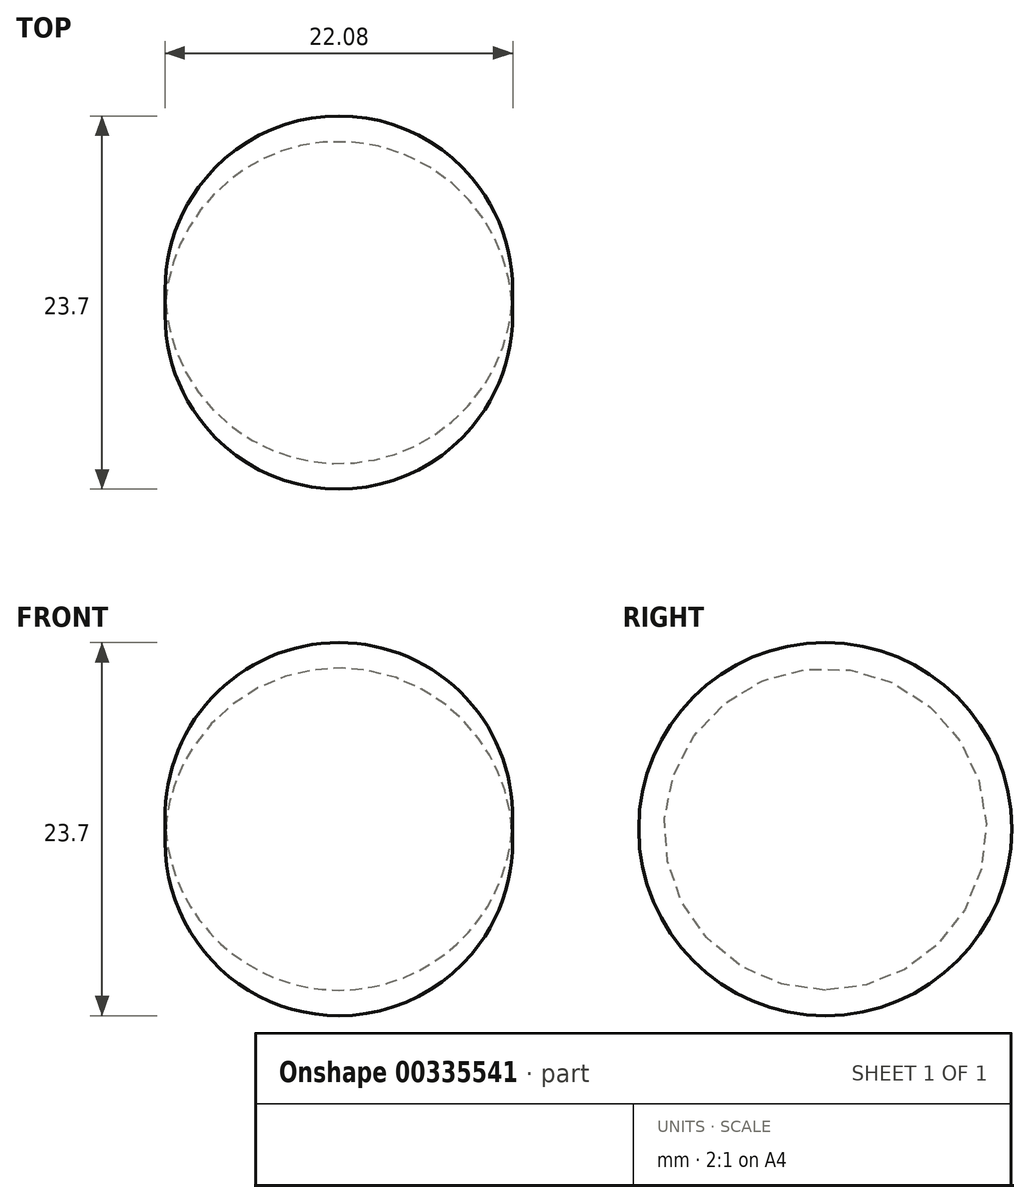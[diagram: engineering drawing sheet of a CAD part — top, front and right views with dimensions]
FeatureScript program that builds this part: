
annotation { "Feature Type Name" : "Feature", "Feature Type Description" : "" }
export const myFeature = defineFeature(function(context is Context, id is Id, definition is map)
    precondition{}
    {
        {
            var Q0;
            Q0=qCreatedBy(makeId("Front.planeOp"),FACE);
            var sketch = newSketch(context, id + "F0", { "sketchPlane" : qUnion([Q0])});
            skLineSegment(sketch, "E0", {"start": v(-11.26, 0) * mm, "end": v(10.77, 0) * mm});
            skLineSegment(sketch, "E1", {"start": v(10.77, 0) * mm, "end": v(-11.26, 0) * mm});
            skPoint(sketch, "E2.orphan", {"position": v(-18.6, 0) * mm});
            skArc(sketch, "E3", {"start": v(10.77, 0) * mm, "mid": v(-0.24, 11.85) * mm, "end": v(-11.26, 0) * mm});
            skSolve(sketch);
        }
        {
            var Q0;
            Q0=makeQuery(id+"F0.imprint","IMPRINT",FACE,{"disambiguationData":[TD([[makeQuery(id+"F0.imprint","IMPRINT",EDGE,{"derivedFrom":sQuery(id+"F0.wireOp",EDGE,"E0")}),1.0]])]});
            var Q1;
            Q1=sQuery(id+"F0.wireOp",EDGE,"E0");
            revolve(context, id + "F1", {"entities" : qUnion([Q0]), "axis" : qUnion([Q1]), "revolveType" : RevolveType.FULL});
        }
    });
